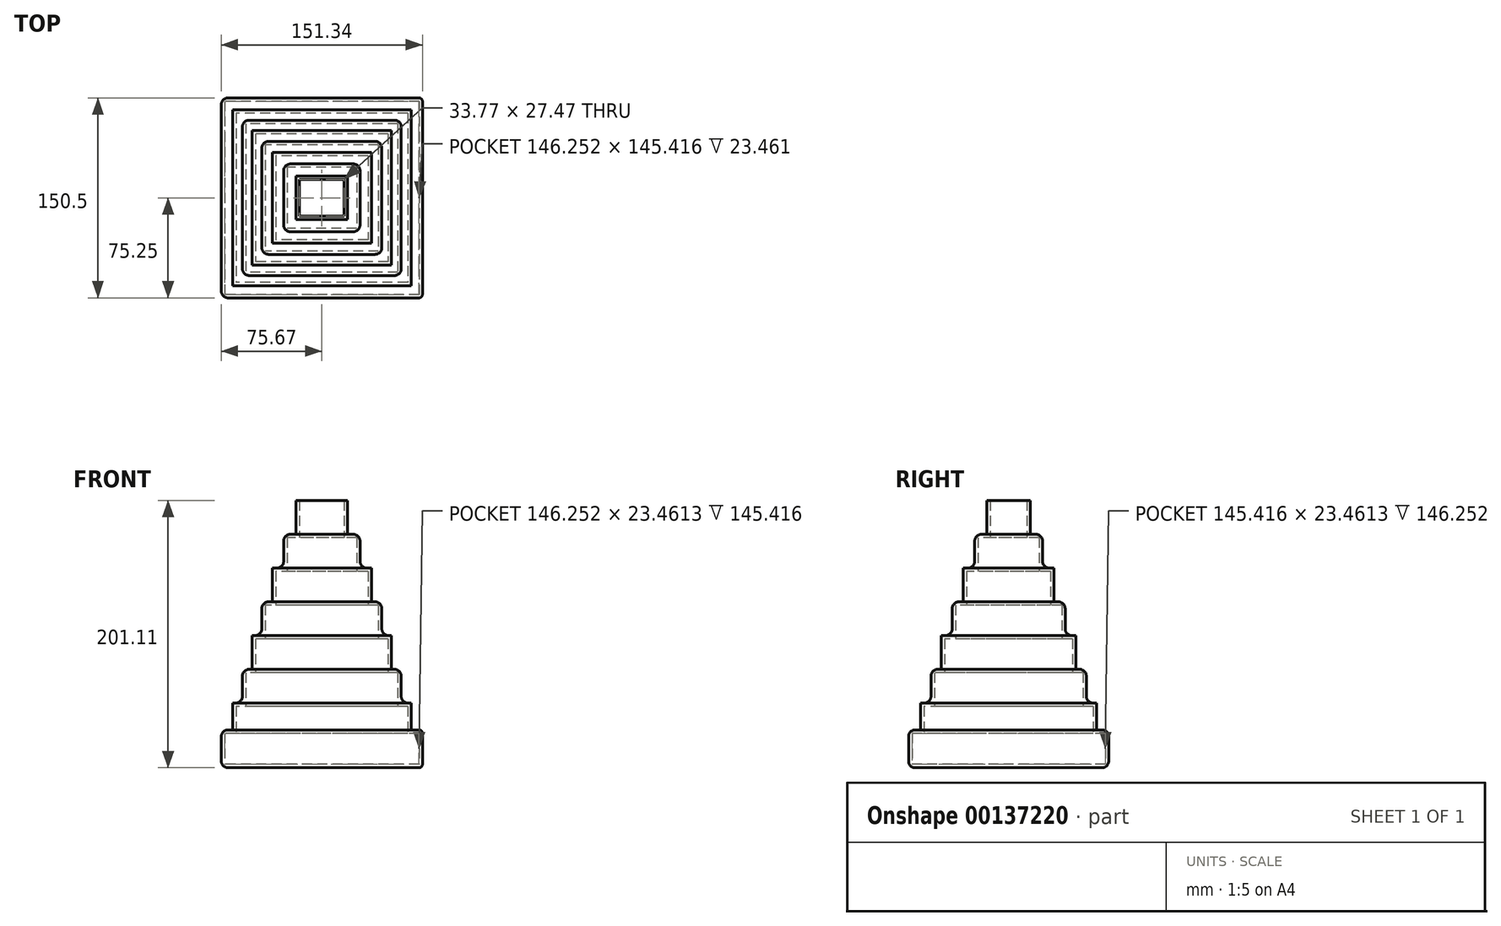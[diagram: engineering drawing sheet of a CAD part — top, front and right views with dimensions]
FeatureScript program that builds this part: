
annotation { "Feature Type Name" : "Feature", "Feature Type Description" : "" }
export const myFeature = defineFeature(function(context is Context, id is Id, definition is map)
    precondition{}
    {
        {
            var Q0;
            Q0=qCreatedBy(makeId("Top.planeOp"),FACE);
            var sketch = newSketch(context, id + "F0", { "sketchPlane" : qUnion([Q0])});
            skLineSegment(sketch, "E0.bottom", {"start": v(75.67, 75.25) * mm, "end": v(-75.67, 75.25) * mm});
            skLineSegment(sketch, "E0.top", {"start": v(75.67, -75.25) * mm, "end": v(-75.67, -75.25) * mm});
            skLineSegment(sketch, "E0.left", {"start": v(75.67, 75.25) * mm, "end": v(75.67, -75.25) * mm});
            skLineSegment(sketch, "E0.right", {"start": v(-75.67, 75.25) * mm, "end": v(-75.67, -75.25) * mm});
            skPoint(sketch, "E0.middle", {"position": v(0, 0) * mm});
            skSolve(sketch);
        }
        {
            var Q0;
            Q0=makeQuery(id+"F0.imprint","IMPRINT",FACE,{"disambiguationData":[TD([[makeQuery(id+"F0.imprint","IMPRINT",EDGE,{"derivedFrom":sQuery(id+"F0.wireOp",EDGE,"E0.bottom")}),1.0]])]});
            extrude(context, id + "F1", {"entities" : qUnion([Q0]), "depth" : 28.54 * mm});
        }
        {
            var Q0;
            Q0=makeQuery(id+"F1.opExtrude","CAP_FACE",FACE,{"disambiguationData":[OSD([sQuery(id+"F0.wireOp",EDGE,"E0.bottom"),sQuery(id+"F0.wireOp",EDGE,"E0.top"),sQuery(id+"F0.wireOp",EDGE,"E0.left"),sQuery(id+"F0.wireOp",EDGE,"E0.right")])],"isStart":false});
            var sketch = newSketch(context, id + "F2", { "sketchPlane" : qUnion([Q0])});
            skLineSegment(sketch, "E1.bottom", {"start": v(67.1, 66.26) * mm, "end": v(-67.1, 66.26) * mm});
            skLineSegment(sketch, "E1.top", {"start": v(67.1, -66.26) * mm, "end": v(-67.1, -66.26) * mm});
            skLineSegment(sketch, "E1.left", {"start": v(67.1, 66.26) * mm, "end": v(67.1, -66.26) * mm});
            skLineSegment(sketch, "E1.right", {"start": v(-67.1, 66.26) * mm, "end": v(-67.1, -66.26) * mm});
            skPoint(sketch, "E1.middle", {"position": v(0, 0) * mm});
            skSolve(sketch);
        }
        {
            var Q0;
            Q0=makeQuery(id+"F2.imprint","IMPRINT",FACE,{"disambiguationData":[TD([[makeQuery(id+"F2.imprint","IMPRINT",EDGE,{"derivedFrom":sQuery(id+"F2.wireOp",EDGE,"E1.bottom")}),1.0]])]});
            extrude(context, id + "F3", {"entities" : qUnion([Q0]), "operationType" : NewBodyOperationType.ADD, "depth" : 20.17 * mm});
        }
        {
            var Q0;
            Q0=makeQuery(id+"F3.opExtrude","CAP_FACE",FACE,{"disambiguationData":[OSD([sQuery(id+"F2.wireOp",EDGE,"E1.bottom"),sQuery(id+"F2.wireOp",EDGE,"E1.top"),sQuery(id+"F2.wireOp",EDGE,"E1.left"),sQuery(id+"F2.wireOp",EDGE,"E1.right")])],"isStart":false});
            var sketch = newSketch(context, id + "F4", { "sketchPlane" : qUnion([Q0])});
            skLineSegment(sketch, "E2.bottom", {"start": v(59.7, 58.45) * mm, "end": v(-59.7, 58.45) * mm});
            skLineSegment(sketch, "E2.top", {"start": v(59.7, -58.45) * mm, "end": v(-59.7, -58.45) * mm});
            skLineSegment(sketch, "E2.left", {"start": v(59.7, 58.45) * mm, "end": v(59.7, -58.45) * mm});
            skLineSegment(sketch, "E2.right", {"start": v(-59.7, 58.45) * mm, "end": v(-59.7, -58.45) * mm});
            skPoint(sketch, "E2.middle", {"position": v(0, 0) * mm});
            skSolve(sketch);
        }
        {
            var Q0;
            Q0=makeQuery(id+"F4.imprint","IMPRINT",FACE,{"disambiguationData":[TD([[makeQuery(id+"F4.imprint","IMPRINT",EDGE,{"derivedFrom":sQuery(id+"F4.wireOp",EDGE,"E2.bottom")}),1.0]])]});
            extrude(context, id + "F5", {"entities" : qUnion([Q0]), "operationType" : NewBodyOperationType.ADD, "depth" : 25.4 * mm});
        }
        {
            var Q0;
            Q0=makeQuery(id+"F5.opExtrude","CAP_FACE",FACE,{"disambiguationData":[OSD([sQuery(id+"F4.wireOp",EDGE,"E2.bottom"),sQuery(id+"F4.wireOp",EDGE,"E2.top"),sQuery(id+"F4.wireOp",EDGE,"E2.left"),sQuery(id+"F4.wireOp",EDGE,"E2.right")])],"isStart":false});
            var sketch = newSketch(context, id + "F6", { "sketchPlane" : qUnion([Q0])});
            skLineSegment(sketch, "E3.bottom", {"start": v(52.46, 50.58) * mm, "end": v(-52.46, 50.58) * mm});
            skLineSegment(sketch, "E3.top", {"start": v(52.46, -50.58) * mm, "end": v(-52.46, -50.58) * mm});
            skLineSegment(sketch, "E3.left", {"start": v(52.46, 50.58) * mm, "end": v(52.46, -50.58) * mm});
            skLineSegment(sketch, "E3.right", {"start": v(-52.46, 50.58) * mm, "end": v(-52.46, -50.58) * mm});
            skPoint(sketch, "E3.middle", {"position": v(0, 0) * mm});
            skSolve(sketch);
        }
        {
            var Q0;
            Q0=makeQuery(id+"F6.imprint","IMPRINT",FACE,{"disambiguationData":[TD([[makeQuery(id+"F6.imprint","IMPRINT",EDGE,{"derivedFrom":sQuery(id+"F6.wireOp",EDGE,"E3.bottom")}),1.0]])]});
            extrude(context, id + "F7", {"entities" : qUnion([Q0]), "operationType" : NewBodyOperationType.ADD, "depth" : 25.4 * mm});
        }
        {
            var Q0;
            Q0=makeQuery(id+"F7.opExtrude","CAP_FACE",FACE,{"disambiguationData":[OSD([sQuery(id+"F6.wireOp",EDGE,"E3.bottom"),sQuery(id+"F6.wireOp",EDGE,"E3.top"),sQuery(id+"F6.wireOp",EDGE,"E3.left"),sQuery(id+"F6.wireOp",EDGE,"E3.right")])],"isStart":false});
            var sketch = newSketch(context, id + "F8", { "sketchPlane" : qUnion([Q0])});
            skLineSegment(sketch, "E4.bottom", {"start": v(45.14, 42.5) * mm, "end": v(-45.14, 42.5) * mm});
            skLineSegment(sketch, "E4.top", {"start": v(45.14, -42.5) * mm, "end": v(-45.14, -42.5) * mm});
            skLineSegment(sketch, "E4.left", {"start": v(45.14, 42.5) * mm, "end": v(45.14, -42.5) * mm});
            skLineSegment(sketch, "E4.right", {"start": v(-45.14, 42.5) * mm, "end": v(-45.14, -42.5) * mm});
            skPoint(sketch, "E4.middle", {"position": v(0, 0) * mm});
            skSolve(sketch);
        }
        {
            var Q0;
            Q0=makeQuery(id+"F8.imprint","IMPRINT",FACE,{"disambiguationData":[TD([[makeQuery(id+"F8.imprint","IMPRINT",EDGE,{"derivedFrom":sQuery(id+"F8.wireOp",EDGE,"E4.bottom")}),1.0]])]});
            extrude(context, id + "F9", {"entities" : qUnion([Q0]), "operationType" : NewBodyOperationType.ADD, "depth" : 25.4 * mm});
        }
        {
            var Q0;
            Q0=makeQuery(id+"F9.opExtrude","CAP_FACE",FACE,{"disambiguationData":[OSD([sQuery(id+"F8.wireOp",EDGE,"E4.bottom"),sQuery(id+"F8.wireOp",EDGE,"E4.top"),sQuery(id+"F8.wireOp",EDGE,"E4.left"),sQuery(id+"F8.wireOp",EDGE,"E4.right")])],"isStart":false});
            var sketch = newSketch(context, id + "F10", { "sketchPlane" : qUnion([Q0])});
            skLineSegment(sketch, "E5.bottom", {"start": v(37.35, 34.08) * mm, "end": v(-37.35, 34.08) * mm});
            skLineSegment(sketch, "E5.top", {"start": v(37.35, -34.08) * mm, "end": v(-37.35, -34.08) * mm});
            skLineSegment(sketch, "E5.left", {"start": v(37.35, 34.08) * mm, "end": v(37.35, -34.08) * mm});
            skLineSegment(sketch, "E5.right", {"start": v(-37.35, 34.08) * mm, "end": v(-37.35, -34.08) * mm});
            skPoint(sketch, "E5.middle", {"position": v(0, 0) * mm});
            skSolve(sketch);
        }
        {
            var Q0;
            Q0=makeQuery(id+"F10.imprint","IMPRINT",FACE,{"disambiguationData":[TD([[makeQuery(id+"F10.imprint","IMPRINT",EDGE,{"derivedFrom":sQuery(id+"F10.wireOp",EDGE,"E5.bottom")}),1.0]])]});
            extrude(context, id + "F11", {"entities" : qUnion([Q0]), "operationType" : NewBodyOperationType.ADD, "depth" : 25.4 * mm});
        }
        {
            var Q0;
            Q0=makeQuery(id+"F11.opExtrude","CAP_FACE",FACE,{"disambiguationData":[OSD([sQuery(id+"F10.wireOp",EDGE,"E5.bottom"),sQuery(id+"F10.wireOp",EDGE,"E5.top"),sQuery(id+"F10.wireOp",EDGE,"E5.left"),sQuery(id+"F10.wireOp",EDGE,"E5.right")])],"isStart":false});
            var sketch = newSketch(context, id + "F12", { "sketchPlane" : qUnion([Q0])});
            skLineSegment(sketch, "E6.bottom", {"start": v(28.72, 25.5) * mm, "end": v(-28.72, 25.5) * mm});
            skLineSegment(sketch, "E6.top", {"start": v(28.72, -25.5) * mm, "end": v(-28.72, -25.5) * mm});
            skLineSegment(sketch, "E6.left", {"start": v(28.72, 25.5) * mm, "end": v(28.72, -25.5) * mm});
            skLineSegment(sketch, "E6.right", {"start": v(-28.72, 25.5) * mm, "end": v(-28.72, -25.5) * mm});
            skPoint(sketch, "E6.middle", {"position": v(0, 0) * mm});
            skSolve(sketch);
        }
        {
            var Q0;
            Q0=makeQuery(id+"F12.imprint","IMPRINT",FACE,{"disambiguationData":[TD([[makeQuery(id+"F12.imprint","IMPRINT",EDGE,{"derivedFrom":sQuery(id+"F12.wireOp",EDGE,"E6.bottom")}),1.0]])]});
            extrude(context, id + "F13", {"entities" : qUnion([Q0]), "operationType" : NewBodyOperationType.ADD, "depth" : 25.4 * mm});
        }
        {
            var Q0;
            Q0=makeQuery(id+"F13.opExtrude","CAP_FACE",FACE,{"disambiguationData":[OSD([sQuery(id+"F12.wireOp",EDGE,"E6.bottom"),sQuery(id+"F12.wireOp",EDGE,"E6.top"),sQuery(id+"F12.wireOp",EDGE,"E6.left"),sQuery(id+"F12.wireOp",EDGE,"E6.right")])],"isStart":false});
            var sketch = newSketch(context, id + "F14", { "sketchPlane" : qUnion([Q0])});
            skLineSegment(sketch, "E7.bottom", {"start": v(19.43, 16.28) * mm, "end": v(-19.43, 16.28) * mm});
            skLineSegment(sketch, "E7.top", {"start": v(19.43, -16.28) * mm, "end": v(-19.43, -16.28) * mm});
            skLineSegment(sketch, "E7.left", {"start": v(19.43, 16.28) * mm, "end": v(19.43, -16.28) * mm});
            skLineSegment(sketch, "E7.right", {"start": v(-19.43, 16.28) * mm, "end": v(-19.43, -16.28) * mm});
            skPoint(sketch, "E7.middle", {"position": v(0, 0) * mm});
            skSolve(sketch);
        }
        {
            var Q0;
            Q0=makeQuery(id+"F14.imprint","IMPRINT",FACE,{"disambiguationData":[TD([[makeQuery(id+"F14.imprint","IMPRINT",EDGE,{"derivedFrom":sQuery(id+"F14.wireOp",EDGE,"E7.bottom")}),1.0]])]});
            extrude(context, id + "F15", {"entities" : qUnion([Q0]), "operationType" : NewBodyOperationType.ADD, "depth" : 25.4 * mm});
        }
        {
            var Q0;
            Q0=makeQuery(id+"F15.opExtrude","CAP_FACE",FACE,{"disambiguationData":[OSD([sQuery(id+"F14.wireOp",EDGE,"E7.bottom"),sQuery(id+"F14.wireOp",EDGE,"E7.top"),sQuery(id+"F14.wireOp",EDGE,"E7.left"),sQuery(id+"F14.wireOp",EDGE,"E7.right")])],"isStart":false});
            shell(context, id + "F16", {"entities" : qUnion([Q0]), "thickness" : 2.54 * mm});
        }
        {
            var Q0;
            Q0=makeQuery(id+"F1.opExtrude","SWEPT_FACE",FACE,{"disambiguationData":[OSD([sQuery(id+"F0.wireOp",EDGE,"E0.left")])]});
            fillet(context, id + "F17", {"entities" : qUnion([Q0]), "radius" : 2.6 * mm, "tangentPropagation" : true, "allowEdgeOverflow" : false});
        }
        {
            var Q0;
            Q0=makeQuery(id+"F1.opExtrude","SWEPT_FACE",FACE,{"disambiguationData":[OSD([sQuery(id+"F0.wireOp",EDGE,"E0.top")])]});
            fillet(context, id + "F18", {"entities" : qUnion([Q0]), "radius" : 5.08 * mm, "tangentPropagation" : true, "allowEdgeOverflow" : false});
        }
        {
            var Q0;
            Q0=makeQuery(id+"F1.opExtrude","SWEPT_FACE",FACE,{"disambiguationData":[OSD([sQuery(id+"F0.wireOp",EDGE,"E0.right")])]});
            fillet(context, id + "F19", {"entities" : qUnion([Q0]), "radius" : 5.08 * mm, "tangentPropagation" : true, "allowEdgeOverflow" : false});
        }
        {
            var Q0;
            Q0=makeQuery(id+"F1.opExtrude","SWEPT_FACE",FACE,{"disambiguationData":[OSD([sQuery(id+"F0.wireOp",EDGE,"E0.bottom")])]});
            fillet(context, id + "F20", {"entities" : qUnion([Q0]), "radius" : 5.08 * mm, "tangentPropagation" : true, "allowEdgeOverflow" : false});
        }
        {
            var Q0;
            Q0=makeQuery(id+"F5.opExtrude","SWEPT_FACE",FACE,{"disambiguationData":[OSD([sQuery(id+"F4.wireOp",EDGE,"E2.bottom")])]});
            var Q1;
            Q1=makeQuery(id+"F9.opExtrude","SWEPT_FACE",FACE,{"disambiguationData":[OSD([sQuery(id+"F8.wireOp",EDGE,"E4.bottom")])]});
            var Q2;
            Q2=makeQuery(id+"F13.opExtrude","SWEPT_FACE",FACE,{"disambiguationData":[OSD([sQuery(id+"F12.wireOp",EDGE,"E6.bottom")])]});
            var Q3;
            Q3=makeQuery(id+"F5.opExtrude","SWEPT_FACE",FACE,{"disambiguationData":[OSD([sQuery(id+"F4.wireOp",EDGE,"E2.left")])]});
            var Q4;
            Q4=makeQuery(id+"F9.opExtrude","SWEPT_FACE",FACE,{"disambiguationData":[OSD([sQuery(id+"F8.wireOp",EDGE,"E4.left")])]});
            var Q5;
            Q5=makeQuery(id+"F13.opExtrude","SWEPT_FACE",FACE,{"disambiguationData":[OSD([sQuery(id+"F12.wireOp",EDGE,"E6.left")])]});
            var Q6;
            Q6=makeQuery(id+"F13.opExtrude","SWEPT_FACE",FACE,{"disambiguationData":[OSD([sQuery(id+"F12.wireOp",EDGE,"E6.right")])]});
            var Q7;
            Q7=makeQuery(id+"F9.opExtrude","SWEPT_FACE",FACE,{"disambiguationData":[OSD([sQuery(id+"F8.wireOp",EDGE,"E4.right")])]});
            var Q8;
            Q8=makeQuery(id+"F5.opExtrude","SWEPT_FACE",FACE,{"disambiguationData":[OSD([sQuery(id+"F4.wireOp",EDGE,"E2.right")])]});
            var Q9;
            Q9=makeQuery(id+"F5.opExtrude","SWEPT_FACE",FACE,{"disambiguationData":[OSD([sQuery(id+"F4.wireOp",EDGE,"E2.top")])]});
            var Q10;
            Q10=makeQuery(id+"F9.opExtrude","SWEPT_FACE",FACE,{"disambiguationData":[OSD([sQuery(id+"F8.wireOp",EDGE,"E4.top")])]});
            var Q11;
            Q11=makeQuery(id+"F13.opExtrude","SWEPT_FACE",FACE,{"disambiguationData":[OSD([sQuery(id+"F12.wireOp",EDGE,"E6.top")])]});
            fillet(context, id + "F21", {"entities" : qUnion([Q0, Q1, Q2, Q3, Q4, Q5, Q6, Q7, Q8, Q9, Q10, Q11]), "radius" : 5.08 * mm, "tangentPropagation" : true, "allowEdgeOverflow" : false});
        }
    });
